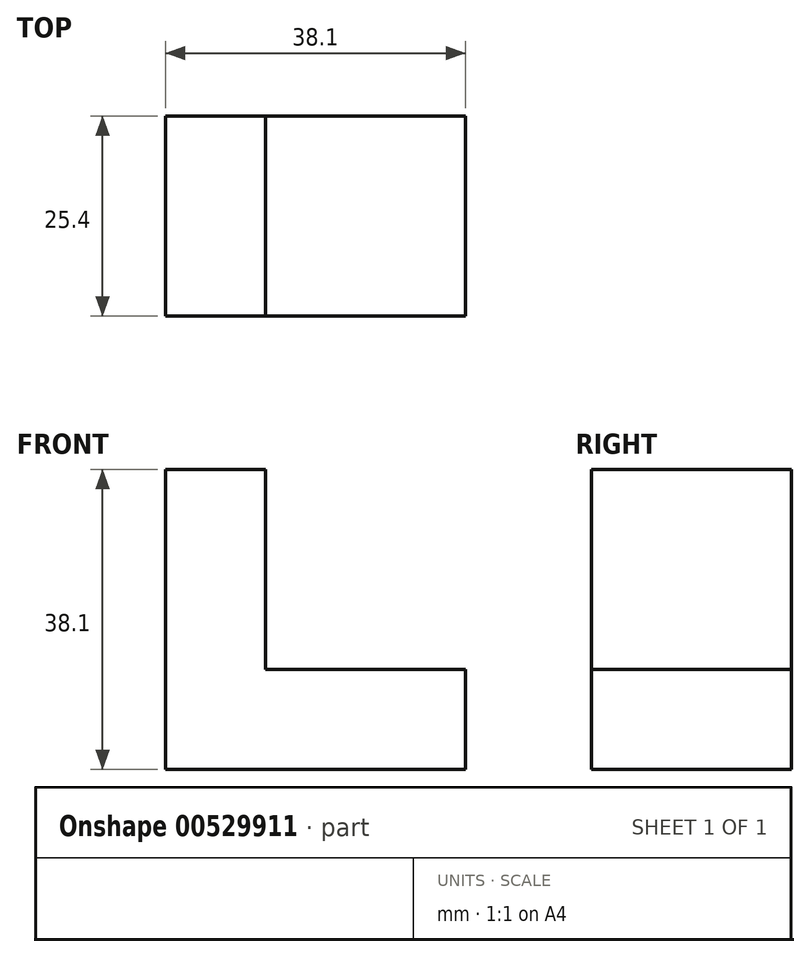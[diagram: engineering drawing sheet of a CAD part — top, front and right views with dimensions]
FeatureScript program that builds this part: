
annotation { "Feature Type Name" : "Feature", "Feature Type Description" : "" }
export const myFeature = defineFeature(function(context is Context, id is Id, definition is map)
    precondition{}
    {
        {
            var Q0;
            Q0=qCreatedBy(makeId("Front.planeOp"),FACE);
            var sketch = newSketch(context, id + "F0", { "sketchPlane" : qUnion([Q0])});
            skLineSegment(sketch, "E0", {"start": v(-67.93, 13.88) * mm, "end": v(-29.83, 13.88) * mm});
            skLineSegment(sketch, "E1", {"start": v(-67.93, 13.88) * mm, "end": v(-67.93, 51.98) * mm});
            skLineSegment(sketch, "E2", {"start": v(-29.83, 13.88) * mm, "end": v(-29.83, 26.58) * mm});
            skLineSegment(sketch, "E3", {"start": v(-67.93, 51.98) * mm, "end": v(-55.23, 51.98) * mm});
            skLineSegment(sketch, "E4", {"start": v(-55.23, 51.98) * mm, "end": v(-55.23, 26.58) * mm});
            skLineSegment(sketch, "E5", {"start": v(-55.23, 26.58) * mm, "end": v(-29.83, 26.58) * mm});
            skSolve(sketch);
        }
        {
            var Q0;
            Q0 = qSketchRegion(id + "F0", true);
            extrude(context, id + "F1", {"entities" : qUnion([Q0]), "depth" : 25.4 * mm, "offsetDistance" : 25.4 * mm});
        }
    });
